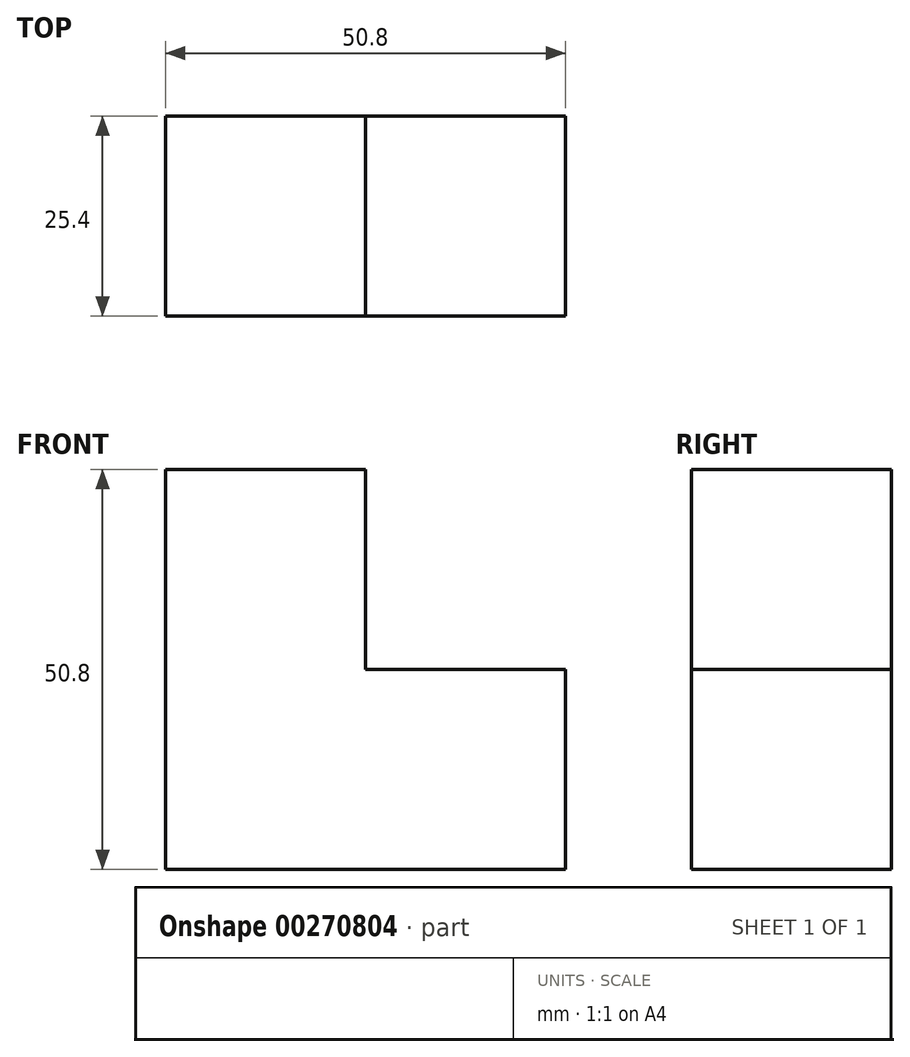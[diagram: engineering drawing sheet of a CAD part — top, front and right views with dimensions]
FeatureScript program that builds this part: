
annotation { "Feature Type Name" : "Feature", "Feature Type Description" : "" }
export const myFeature = defineFeature(function(context is Context, id is Id, definition is map)
    precondition{}
    {
        {
            var Q0;
            Q0=qCreatedBy(makeId("Front.planeOp"),FACE);
            var sketch = newSketch(context, id + "F0", { "sketchPlane" : qUnion([Q0])});
            skLineSegment(sketch, "E0", {"start": v(0, 0) * mm, "end": v(-50.8, 0) * mm});
            skLineSegment(sketch, "E1", {"start": v(-50.8, 0) * mm, "end": v(-50.8, 50.8) * mm});
            skLineSegment(sketch, "E2", {"start": v(-50.8, 50.8) * mm, "end": v(-25.4, 50.8) * mm});
            skLineSegment(sketch, "E3", {"start": v(-25.4, 50.8) * mm, "end": v(-25.4, 25.4) * mm});
            skLineSegment(sketch, "E4", {"start": v(-25.4, 25.4) * mm, "end": v(0, 25.4) * mm});
            skLineSegment(sketch, "E5", {"start": v(0, 25.4) * mm, "end": v(0, 0) * mm});
            skSolve(sketch);
        }
        {
            var Q0;
            Q0=makeQuery(id+"F0.imprint","IMPRINT",FACE,{"disambiguationData":[TD([[makeQuery(id+"F0.imprint","IMPRINT",EDGE,{"derivedFrom":sQuery(id+"F0.wireOp",EDGE,"E0")}),-1.0]])]});
            extrude(context, id + "F1", {"entities" : qUnion([Q0]), "depth" : 25.4 * mm});
        }
    });
